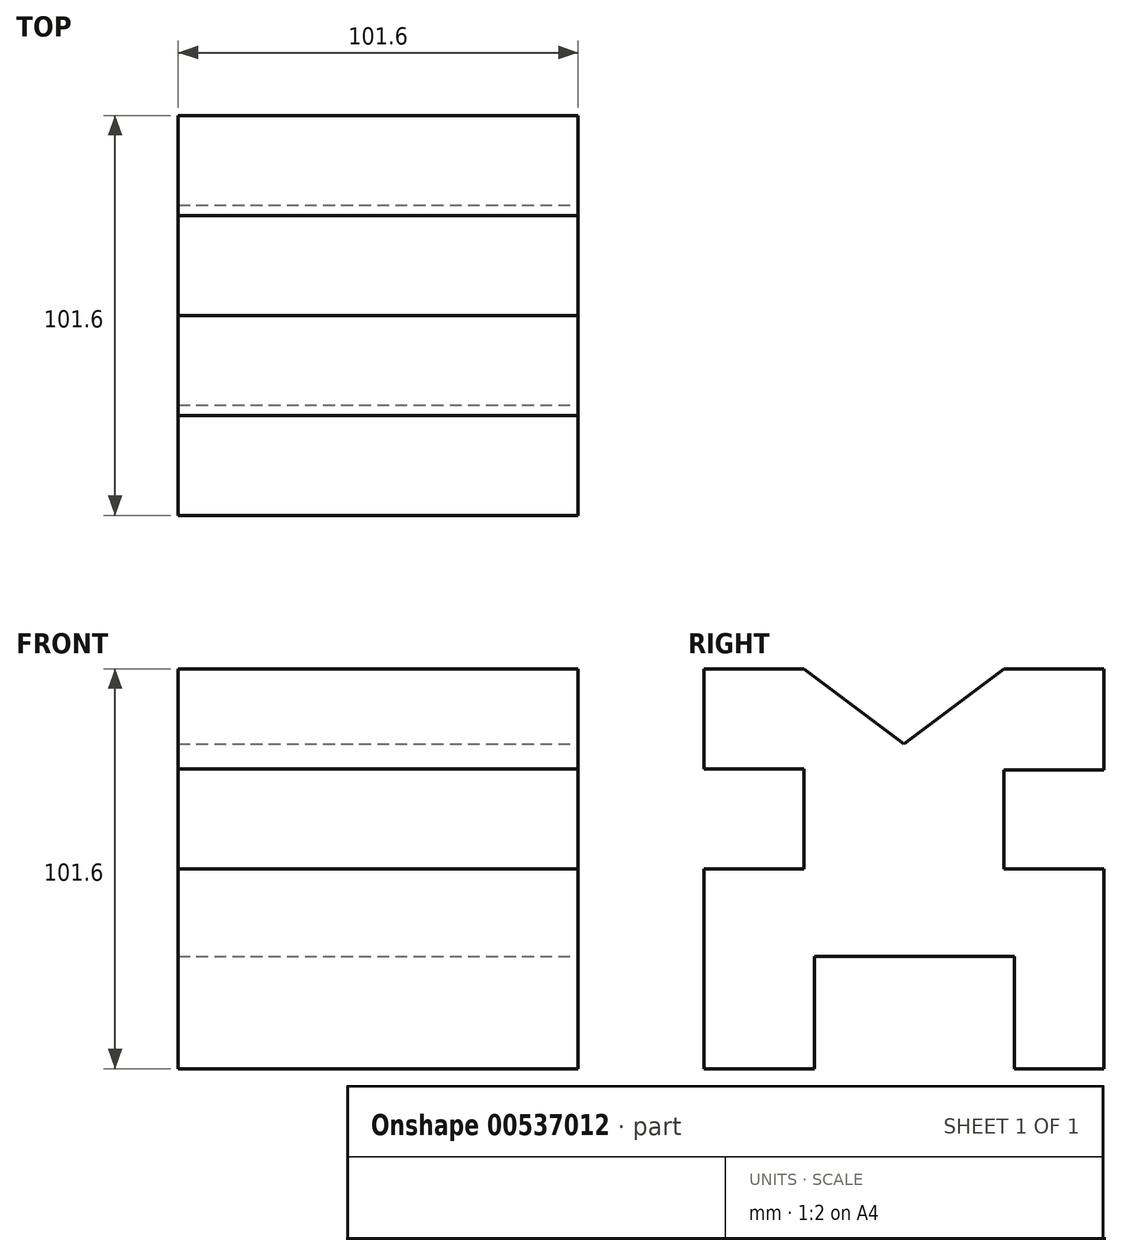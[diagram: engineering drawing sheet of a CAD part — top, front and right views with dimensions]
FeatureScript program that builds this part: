
annotation { "Feature Type Name" : "Feature", "Feature Type Description" : "" }
export const myFeature = defineFeature(function(context is Context, id is Id, definition is map)
    precondition{}
    {
        {
            var Q0;
            Q0=qCreatedBy(makeId("Top.planeOp"),FACE);
            var sketch = newSketch(context, id + "F0", { "sketchPlane" : qUnion([Q0])});
            skLineSegment(sketch, "E0.bottom", {"start": v(0, 0) * mm, "end": v(-101.6, 0) * mm});
            skLineSegment(sketch, "E0.top", {"start": v(0, -101.6) * mm, "end": v(-101.6, -101.6) * mm});
            skLineSegment(sketch, "E0.left", {"start": v(0, 0) * mm, "end": v(0, -101.6) * mm});
            skLineSegment(sketch, "E0.right", {"start": v(-101.6, 0) * mm, "end": v(-101.6, -101.6) * mm});
            skSolve(sketch);
        }
        {
            var Q0;
            Q0=makeQuery(id+"F0.imprint","IMPRINT",FACE,{"disambiguationData":[TD([[makeQuery(id+"F0.imprint","IMPRINT",EDGE,{"derivedFrom":sQuery(id+"F0.wireOp",EDGE,"E0.bottom")}),1.0]])]});
            extrude(context, id + "F1", {"entities" : qUnion([Q0]), "depth" : 101.6 * mm, "offsetDistance" : 25.4 * mm});
        }
        {
            var Q0;
            Q0=makeQuery(id+"F1.opExtrude","SWEPT_FACE",FACE,{"disambiguationData":[OSD([sQuery(id+"F0.wireOp",EDGE,"E0.top")])]});
            var sketch = newSketch(context, id + "F2", { "sketchPlane" : qUnion([Q0])});
            skLineSegment(sketch, "E1.bottom", {"start": v(-101.6, 76.2) * mm, "end": v(0, 76.2) * mm});
            skLineSegment(sketch, "E1.top", {"start": v(-101.6, 50.8) * mm, "end": v(0, 50.8) * mm});
            skLineSegment(sketch, "E1.left", {"start": v(-101.6, 76.2) * mm, "end": v(-101.6, 50.8) * mm});
            skLineSegment(sketch, "E1.right", {"start": v(0, 76.2) * mm, "end": v(0, 50.8) * mm});
            skSolve(sketch);
        }
        {
            var Q0;
            Q0=makeQuery(id+"F2.imprint","IMPRINT",FACE,{"disambiguationData":[TD([[makeQuery(id+"F2.imprint","IMPRINT",EDGE,{"derivedFrom":sQuery(id+"F2.wireOp",EDGE,"E1.bottom")}),-1.0]])]});
            extrude(context, id + "F3", {"entities" : qUnion([Q0]), "operationType" : NewBodyOperationType.REMOVE, "oppositeDirection" : true, "depth" : 25.4 * mm, "offsetDistance" : 25.4 * mm});
        }
        {
            var Q0;
            Q0=makeQuery(id+"F1.opExtrude","SWEPT_FACE",FACE,{"disambiguationData":[OSD([sQuery(id+"F0.wireOp",EDGE,"E0.left")])]});
            var sketch = newSketch(context, id + "F4", { "sketchPlane" : qUnion([Q0])});
            skLineSegment(sketch, "E2.bottom", {"start": v(-73.53, 0) * mm, "end": v(-22.73, 0) * mm});
            skLineSegment(sketch, "E2.top", {"start": v(-73.53, 28.55) * mm, "end": v(-22.73, 28.55) * mm});
            skLineSegment(sketch, "E2.left", {"start": v(-73.53, 0) * mm, "end": v(-73.53, 28.55) * mm});
            skLineSegment(sketch, "E2.right", {"start": v(-22.73, 0) * mm, "end": v(-22.73, 28.55) * mm});
            skSolve(sketch);
        }
        {
            var Q0;
            Q0=makeQuery(id+"F4.imprint","IMPRINT",FACE,{"disambiguationData":[TD([[makeQuery(id+"F4.imprint","IMPRINT",EDGE,{"derivedFrom":sQuery(id+"F4.wireOp",EDGE,"E2.bottom")}),-1.0]])]});
            extrude(context, id + "F5", {"entities" : qUnion([Q0]), "operationType" : NewBodyOperationType.REMOVE, "oppositeDirection" : true, "depth" : 25.4 * mm, "offsetDistance" : 25.4 * mm});
        }
        {
            var Q0;
            Q0=makeQuery(id+"F5.boolean.opBoolean","COPY",FACE,{"derivedFrom":makeQuery(id+"F5.opExtrude","CAP_FACE",FACE,{"disambiguationData":[OSD([sQuery(id+"F4.wireOp",EDGE,"E2.bottom"),sQuery(id+"F4.wireOp",EDGE,"E2.top"),sQuery(id+"F4.wireOp",EDGE,"E2.left"),sQuery(id+"F4.wireOp",EDGE,"E2.right")])],"isStart":false})});
            extrude(context, id + "F6", {"entities" : qUnion([Q0]), "operationType" : NewBodyOperationType.REMOVE, "oppositeDirection" : true, "depth" : 180.6 * mm, "offsetDistance" : 25.4 * mm});
        }
        {
            var Q0;
            Q0=makeQuery(id+"F1.opExtrude","SWEPT_FACE",FACE,{"disambiguationData":[OSD([sQuery(id+"F0.wireOp",EDGE,"E0.right")])]});
            var sketch = newSketch(context, id + "F7", { "sketchPlane" : qUnion([Q0])});
            skLineSegment(sketch, "E3.bottom", {"start": v(0, 76.47) * mm, "end": v(25.4, 76.47) * mm});
            skLineSegment(sketch, "E3.top", {"start": v(0, 51.9) * mm, "end": v(25.4, 51.9) * mm});
            skLineSegment(sketch, "E3.left", {"start": v(0, 76.47) * mm, "end": v(0, 51.9) * mm});
            skLineSegment(sketch, "E3.right", {"start": v(25.4, 76.47) * mm, "end": v(25.4, 51.9) * mm});
            skSolve(sketch);
        }
        {
            var Q0;
            Q0=makeQuery(id+"F7.imprint","IMPRINT",FACE,{"disambiguationData":[TD([[makeQuery(id+"F7.imprint","IMPRINT",EDGE,{"derivedFrom":sQuery(id+"F7.wireOp",EDGE,"E3.bottom")}),-1.0]])]});
            extrude(context, id + "F8", {"entities" : qUnion([Q0]), "operationType" : NewBodyOperationType.REMOVE, "depth" : 25.4 * mm, "offsetDistance" : 25.4 * mm});
        }
        {
            var Q0;
            Q0=makeQuery(id+"F1.opExtrude","SWEPT_FACE",FACE,{"disambiguationData":[OSD([sQuery(id+"F0.wireOp",EDGE,"E0.bottom")])]});
            var sketch = newSketch(context, id + "F9", { "sketchPlane" : qUnion([Q0])});
            skLineSegment(sketch, "E4.bottom", {"start": v(0, 75.94) * mm, "end": v(101.6, 75.94) * mm});
            skLineSegment(sketch, "E4.top", {"start": v(0, 50.8) * mm, "end": v(101.6, 50.8) * mm});
            skLineSegment(sketch, "E4.left", {"start": v(0, 75.94) * mm, "end": v(0, 50.8) * mm});
            skLineSegment(sketch, "E4.right", {"start": v(101.6, 75.94) * mm, "end": v(101.6, 50.8) * mm});
            skSolve(sketch);
        }
        {
            var Q0;
            Q0=makeQuery(id+"F9.imprint","IMPRINT",FACE,{"disambiguationData":[TD([[makeQuery(id+"F9.imprint","IMPRINT",EDGE,{"derivedFrom":sQuery(id+"F9.wireOp",EDGE,"E4.bottom")}),-1.0]])]});
            extrude(context, id + "F10", {"entities" : qUnion([Q0]), "operationType" : NewBodyOperationType.REMOVE, "oppositeDirection" : true, "depth" : 25.4 * mm, "offsetDistance" : 25.4 * mm});
        }
        {
            var Q0;
            Q0=makeQuery(id+"F1.opExtrude","SWEPT_FACE",FACE,{"disambiguationData":[OSD([sQuery(id+"F0.wireOp",EDGE,"E0.left")])]});
            var sketch = newSketch(context, id + "F11", { "sketchPlane" : qUnion([Q0])});
            skLineSegment(sketch, "E5", {"start": v(-101.6, 101.6) * mm, "end": v(-76.2, 101.6) * mm});
            skLineSegment(sketch, "E6", {"start": v(-76.2, 101.6) * mm, "end": v(-50.8, 101.6) * mm});
            skLineSegment(sketch, "E7", {"start": v(-50.8, 101.6) * mm, "end": v(-25.4, 101.6) * mm});
            skLineSegment(sketch, "E8", {"start": v(-25.4, 101.6) * mm, "end": v(-50.8, 82.53) * mm});
            skLineSegment(sketch, "E9", {"start": v(-50.8, 82.53) * mm, "end": v(-76.2, 101.6) * mm});
            skSolve(sketch);
        }
        {
            var Q0;
            Q0=makeQuery(id+"F11.imprint","IMPRINT",FACE,{"disambiguationData":[TD([[makeQuery(id+"F11.imprint","IMPRINT",EDGE,{"derivedFrom":sQuery(id+"F11.wireOp",EDGE,"E6")}),1.0]])]});
            extrude(context, id + "F12", {"entities" : qUnion([Q0]), "operationType" : NewBodyOperationType.REMOVE, "oppositeDirection" : true, "depth" : 170.7 * mm, "offsetDistance" : 25.4 * mm});
        }
    });
